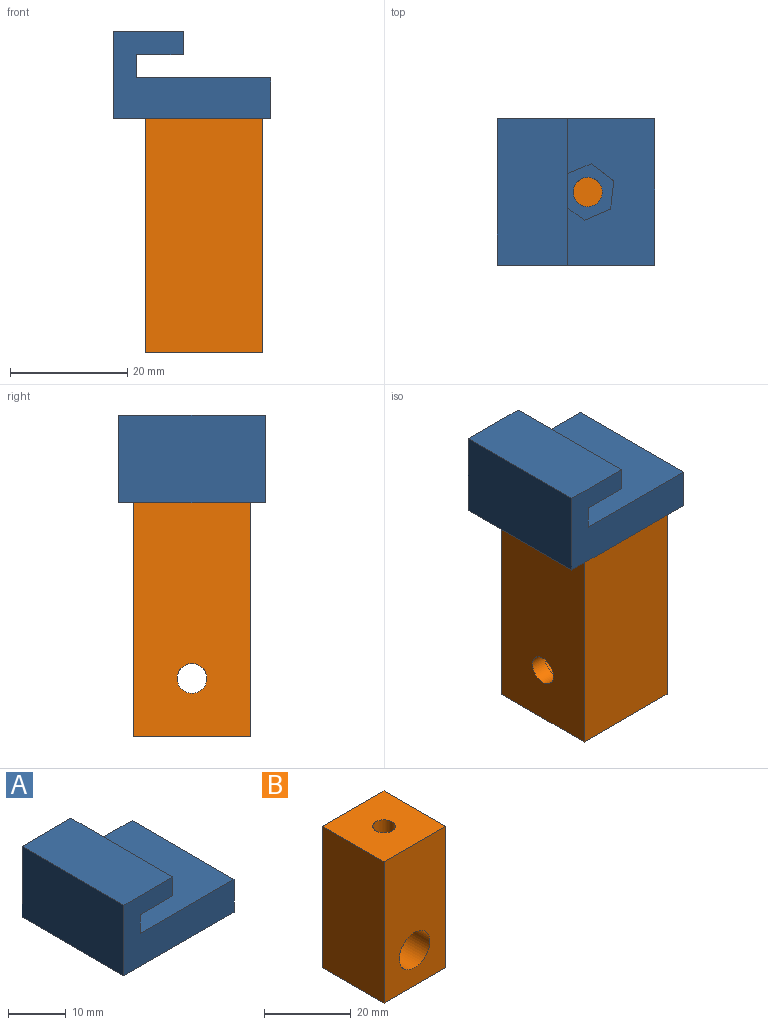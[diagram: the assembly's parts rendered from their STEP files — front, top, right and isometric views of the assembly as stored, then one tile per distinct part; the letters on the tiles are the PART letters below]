
ASSEMBLY  parts=2 mates=1
PART A: 18 faces, bbox 27x25x15 mm
  f0: plane 27x25mm, normal (0,0,-1), area 655.4mm2, adj f1,f7,f8,f9,f17
  f1: plane 25x7mm, normal (1,0,0), area 175mm2, adj f0,f2,f8,f9
  f2: plane 25x23mm, normal (0,0,1), area 513.4mm2, adj f1,f3,f8,f9,f10,f11,f12,f13
  f3: plane 25x4mm, normal (1,0,0), area 100mm2, adj f2,f4,f8,f9
  f4: plane 25x8mm, normal (0,0,-1), area 200mm2, adj f3,f5,f8,f9
  f5: plane 25x4mm, normal (1,0,0), area 100mm2, adj f4,f6,f8,f9
  f6: plane 25x12mm, normal (0,0,1), area 300mm2, adj f5,f7,f8,f9
  f7: plane 25x15mm, normal (-1,0,0), area 375mm2, adj f0,f6,f8,f9
  f8: plane 27x15mm, normal (0,-1,0), area 253mm2, adj f0,f1,f2,f3,f4,f5,f6,f7
  f9: plane 27x15mm, normal (0,1,0), area 253mm2, adj f0,f1,f2,f3,f4,f5,f6,f7
  f10: plane 4x3.91mm, normal (-0.6,-0.8,0), area 19.5mm2, adj f2,f11,f15,f16
  f11: plane 4.47x4mm, normal (0.4,-0.92,0), area 19.5mm2, adj f2,f10,f12,f16
  f12: plane 4.84x4mm, normal (0.99,-0.12,0), area 19.5mm2, adj f2,f11,f13,f16
  f13: plane 4x3.91mm, normal (0.6,0.8,0), area 19.5mm2, adj f2,f12,f14,f16
  f14: plane 4.47x4mm, normal (-0.4,0.92,0), area 19.5mm2, adj f2,f13,f15,f16
  f15: plane 4.84x4mm, normal (-0.99,0.12,0), area 19.5mm2, adj f2,f10,f14,f16
  f16: plane 9.68x8.95mm, normal (0,0,1), area 42mm2, adj f10,f11,f12,f13,f14,f15,f17
  f17: cylinder r=2.5mm len=5mm, axis (0,0,1), area 47.1mm2, adj f0,f16
PART B: 11 faces, bbox 20x20x40 mm
  f0: cylinder r=2.55mm len=5.1mm, axis (0,-1,0), area 48.1mm2, adj f1,f8
  f1: plane 40x20mm, normal (0,1,0), area 779.6mm2, adj f0,f2,f4,f5,f6
  f2: plane 40x20mm, normal (-1,0,0), area 800mm2, adj f1,f3,f5,f6
  f3: plane 40x20mm, normal (0,-1,0), area 721.5mm2, adj f2,f4,f5,f6,f7
  f4: plane 40x20mm, normal (1,0,0), area 800mm2, adj f1,f3,f5,f6
  f5: plane 20x20mm, normal (0,0,1), area 378.8mm2, adj f1,f2,f3,f4,f9
  f6: plane 20x20mm, normal (0,0,-1), area 400mm2, adj f1,f2,f3,f4
  f7: cylinder r=5mm len=17mm, axis (0,-1,0), area 534.1mm2, adj f3,f8
  f8: plane 10x10mm, normal (0,-1,0), area 58.1mm2, adj f0,f7
  f9: cylinder r=2.6mm len=20mm, axis (0,0,1), area 326.7mm2, adj f5,f10
  f10: plane 5.2x5.2mm, normal (0,0,1), area 21.2mm2, adj f9
PLACE A t=(-14.42,13.7,-17.5)mm
PLACE B rot(axis=(0,0,1),90deg) t=(24.92,35.8,-28.64)mm
MATE slider B.f9 <-> A.f17  axis (0,0,1) through (-17.69,1.2,11.36)mm
